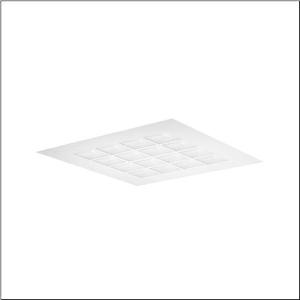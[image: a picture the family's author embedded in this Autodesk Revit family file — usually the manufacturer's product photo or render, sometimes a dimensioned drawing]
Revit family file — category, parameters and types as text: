
# Revit family: scriptus_r__11_5mz312ledzm00191xx_ec59
name_source: partatom
category: Lighting Fixtures
units: mm (PartAtom-declared; Revit-internal decimal feet)

## family parameters
Cut with Voids When Loaded = No
Host = Face
Light Source = No
Part Type = Normal
Room Calculation Point = No
Round Connector Dimension = Use Diameter
Shared = No

## types (1)
- --- (1 x LED, 6400 lm, 43 W, 4000K)
    Apparent Load = 43 VA
    CIE Flux Codes = 80 95 99 100 100
    Color Rendering = 80
    Color Temperature = 4000K
    Default Elevation = 1800 mm
    Description = Scriptus® 11, office luminaire, primary optical cover: lenses, CAT 2 (L<= 3000cd/m²), light emission: direct distribution, primary light characteristic: symmetric, installation type: lay-in mounting, LED, rated luminous flux: 6.400lm, light colour: 840, colour temperature: 4000K, control gear: ECG DALI, with terminal, 3+2-pole, max. 2.5mm², mains connection: 230V, AC, 50Hz, housing, of sheet steel, galvanised, traffic white (RAL 9016), module: M625, length: 621mm, width: 621mm, height: 68mm, protection rating (complete): IP20, insulation class (complete): insulation class I (protective earthing), certification: CE, impact resistance: IK02, permissible operating ambient temperature: 0..+35°C, standard: EN 50419, packaging unit: 1 piece
    Height = 80 mm  [stored 0.262467 ft]
    Lamp = 1 x LED
    Lamp Light Flux = 6400 lm
    Lamp Power = 43 W
    Lamp count = 1
    Length = 622 mm
    Luminous efficacy = 149 lm/W
    Manufacturer = Siteco
    ModVariant = No
    Model = 5MZ312LEDZM00191XX
    Mounting Place = Ceiling
    Mounting Type = Pendant
    Number of Poles = 1
    OnlyDefault = Yes
    Power Factor = 1
    Product Name = Scriptus® 11
    Product group = office luminaire | ceiling pendant
    ProductGroupID = 902
    Protection Class = Protection class I
    Protection Degree = IP 20
    RLX_Detail_Level = 1
    RLX_Emergency_Light_Flux = 0 lm
    RLX_Emergency_Type = 0
    RLX_Emergency_Type_DB = No
    RlxData = <blob elided: 22733 chars, md5=7f126a33>
    Socket = socket
    Standby Power = 0 W
    System Light Flux = 6400 lm
    System Power = 43 W
    Type Comments = factory setting: luminous flux: 100 % | dim-lin: 254 | 227 mA
    Type Image = l_1006857.jpg
    URL = http://relux.com
    VarID = @adj_148909
    Voltage = 0 V
    Weight = 0.00 kg
    Width = 622 mm

note: [stored X ft] marks values corroborated as IEEE doubles in the binary element streams (Revit-internal decimal feet)

## geometry (parser evidence)
native form markers: Blend x4, Sweep x9
no freeform markers — native parametric forms only
